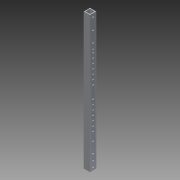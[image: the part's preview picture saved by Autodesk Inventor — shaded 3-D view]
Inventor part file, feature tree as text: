
AUTODESK INVENTOR PART (.ipt)
format: ipt  version: 2013 (Build 170138000, 138)  size: 222,720 bytes
history: native  units: in
note: dims shown in document units (in); Inventor stores cm internally (conversion verified against a paired STEP export)
features: extrude x4, sketch x4
ambient origin geometry x8: Origin, YZ Plane, XZ Plane, XY Plane, X Axis, Y Axis, Z Axis, Center Point
bodies: Solid1 (feature_tree)
feature tree (8):
  extrude  "Extrusion1"  Depth=1.0in
  extrude  "Extrusion2"  Depth=22.0in TaperAngle=0.0deg
  extrude  "Extrusion3"  Depth=0.26in
  extrude  "Extrusion4"  Depth=11.0236in
  sketch  "Sketch1"  dims[d0=1.0in d1=1.0in]
  sketch  "Sketch2"  dims[d2=0.125in d3=22.0in d4=0.0in]
  sketch  "Sketch3"  dims[d5=0.55in d6=0.26in]
  sketch  "Sketch4"  dims[d7=22.0in d8=11.0236in d10=0.7741in d11=0.3937in d13=1.0in d15=1.0in d16=0.0in d17=1.75in d18=2.0in d19=1.75in d20=1.75in d21=0.26in d22=0.26in d23=0.26in d24=0.26in d25=0.26in d26=0.26in d27=0.26in d28=0.26in d29=1.0in d30=0.0in d31=2.0in d32=0.26in d33=0.26in d40=0.5in d41=0.26in d42=0.5in d43=0.26in d46=0.75in d47=0.75in d48=0.26in d49=0.26in d50=1.0in d51=0.0in d52=0.26in d53=5.5in d64=1.0in d65=0.26in d66=0.55in d67=22.0in d68=11.0236in d70=0.7741in d71=0.3937in d73=1.0in d76=0.375in d77=0.375in d78=1.9685in d80=0.75in d81=0.3937in d83=1.0in d85=0.5in d86=2.3622in d88=0.75in d89=0.3937in d91=1.0in]
